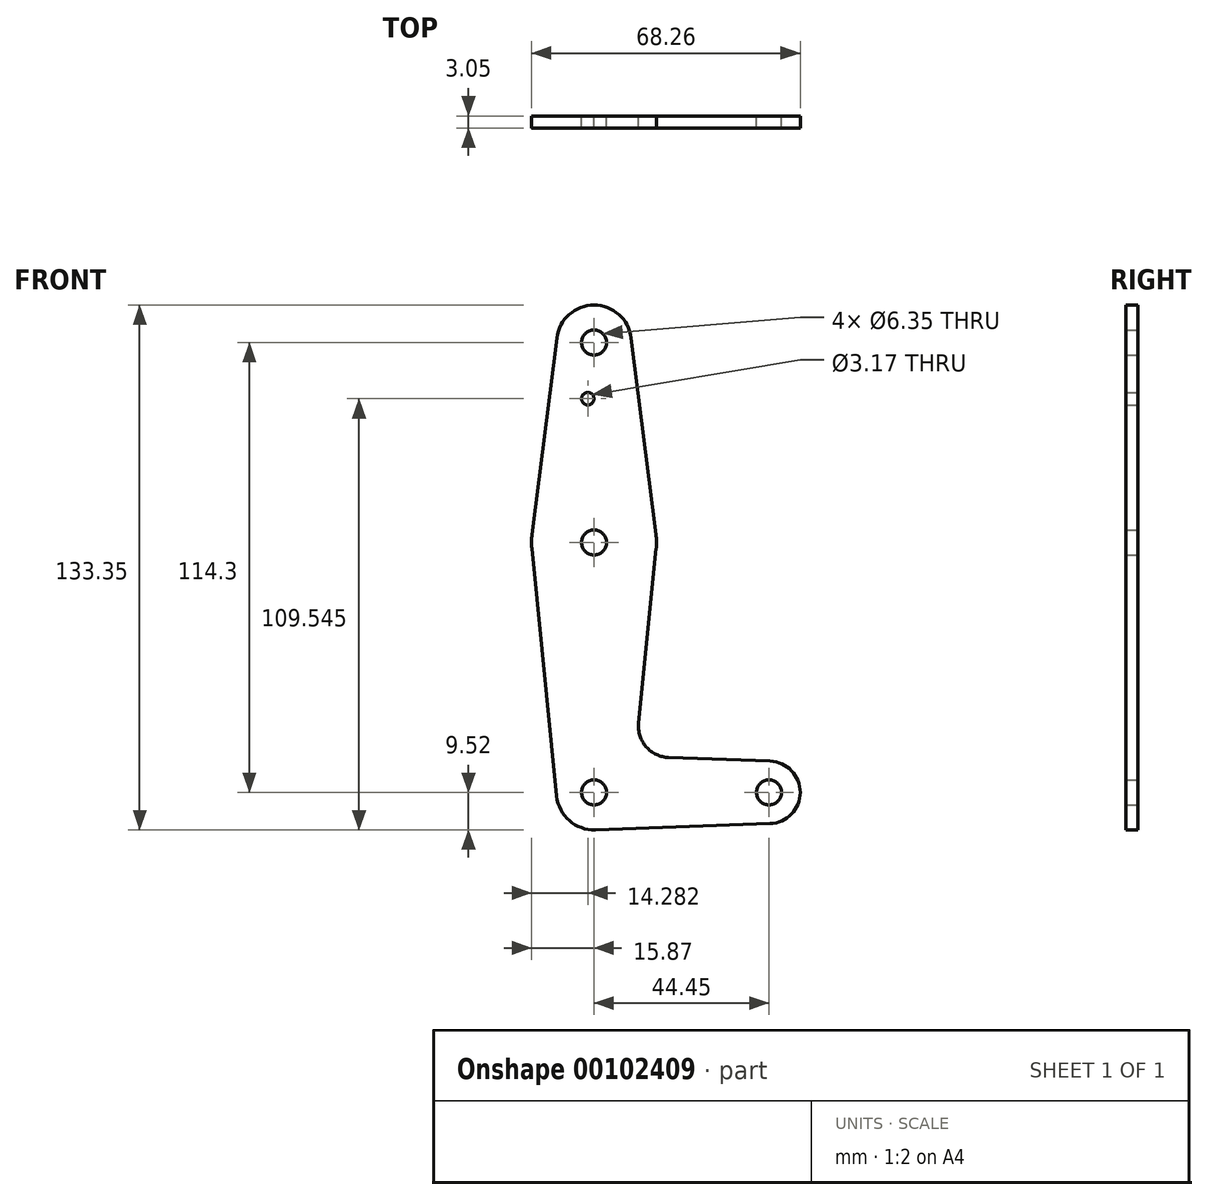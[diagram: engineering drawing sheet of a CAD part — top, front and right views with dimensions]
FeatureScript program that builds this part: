
annotation { "Feature Type Name" : "Feature", "Feature Type Description" : "" }
export const myFeature = defineFeature(function(context is Context, id is Id, definition is map)
    precondition{}
    {
        {
            var Q0;
            Q0=qCreatedBy(makeId("Front.planeOp"),FACE);
            var sketch = newSketch(context, id + "F0", { "sketchPlane" : qUnion([Q0])});
            skLineSegment(sketch, "E0", {"start": v(0, 0) * mm, "end": v(0, 114.3) * mm, "construction": true});
            skLineSegment(sketch, "E1", {"start": v(0, 0) * mm, "end": v(44.45, 0) * mm, "construction": true});
            skCircle(sketch, "E2", {"center": v(0, 114.3) * mm, "radius": 9.53 * mm});
            skCircle(sketch, "E3", {"center": v(0, 0) * mm, "radius": 9.53 * mm});
            skCircle(sketch, "E4", {"center": v(44.45, 0) * mm, "radius": 7.94 * mm});
            skCircle(sketch, "E5", {"center": v(0, 63.5) * mm, "radius": 15.88 * mm});
            skLineSegment(sketch, "E6", {"start": v(-15.75, 65.48) * mm, "end": v(-9.45, 115.5) * mm});
            skLineSegment(sketch, "E7", {"start": v(9.45, 115.5) * mm, "end": v(15.75, 65.48) * mm});
            skLineSegment(sketch, "E8", {"start": v(15.8, 61.91) * mm, "end": v(11.34, 17.59) * mm});
            skLineSegment(sketch, "E9", {"start": v(18.97, 8.85) * mm, "end": v(44.73, 7.93) * mm});
            skLineSegment(sketch, "E10", {"start": v(0.34, -9.52) * mm, "end": v(44.73, -7.93) * mm});
            skCircle(sketch, "E11", {"center": v(0, 114.3) * mm, "radius": 3.18 * mm});
            skCircle(sketch, "E12", {"center": v(-1.59, 100.03) * mm, "radius": 1.59 * mm});
            skCircle(sketch, "E13", {"center": v(0, 63.5) * mm, "radius": 3.18 * mm});
            skCircle(sketch, "E14", {"center": v(0, 0) * mm, "radius": 3.18 * mm});
            skCircle(sketch, "E15", {"center": v(44.45, 0) * mm, "radius": 3.18 * mm});
            skArc(sketch, "E16.filletArc", {"start": v(11.34, 17.59) * mm, "mid": v(13.26, 11.57) * mm, "end": v(18.97, 8.85) * mm});
            skLineSegment(sketch, "E17", {"start": v(-15.8, 61.91) * mm, "end": v(-9.48, -0.95) * mm});
            skSolve(sketch);
        }
        {
            var Q0;
            Q0 = qSketchRegion(id + "F0", true);
            extrude(context, id + "F1", {"entities" : qUnion([Q0]), "depth" : 3.05 * mm});
        }
    });
